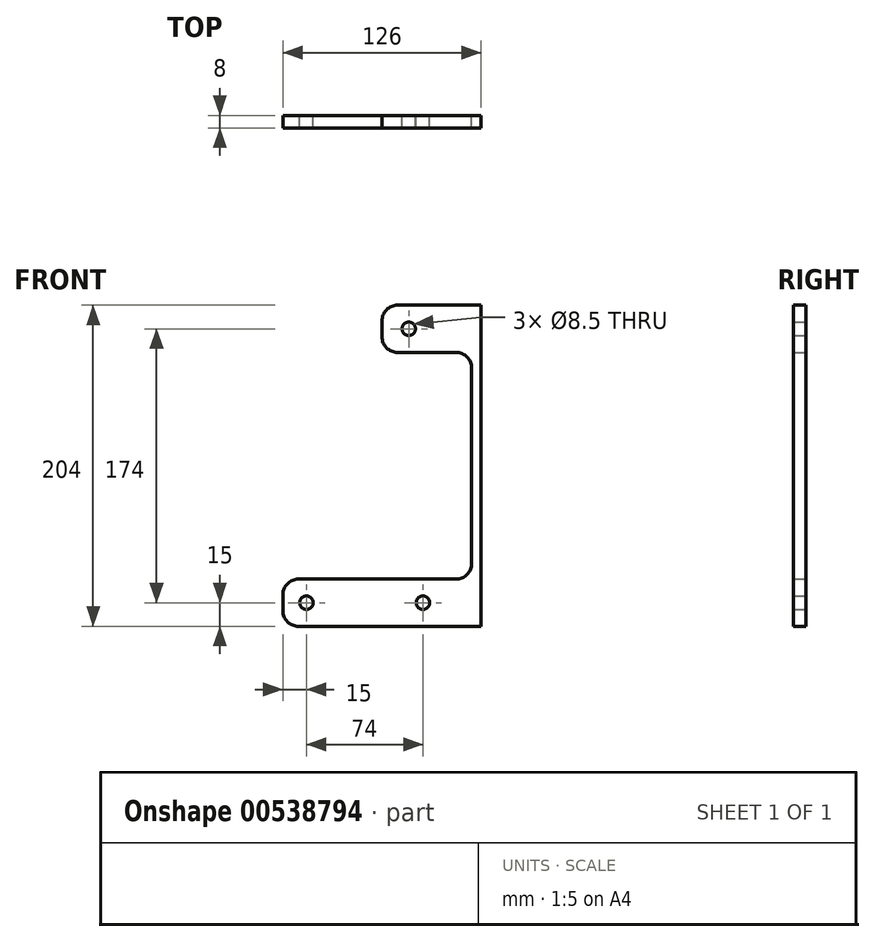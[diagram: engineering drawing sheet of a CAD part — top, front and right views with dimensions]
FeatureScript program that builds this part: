
annotation { "Feature Type Name" : "Feature", "Feature Type Description" : "" }
export const myFeature = defineFeature(function(context is Context, id is Id, definition is map)
    precondition{}
    {
        {
            var Q0;
            Q0=qCreatedBy(makeId("Front.planeOp"),FACE);
            var sketch = newSketch(context, id + "F0", { "sketchPlane" : qUnion([Q0])});
            skLineSegment(sketch, "E0", {"start": v(0, 0) * mm, "end": v(0, -183.01) * mm});
            skCircle(sketch, "E1", {"center": v(-46, 0) * mm, "radius": 4.25 * mm});
            skCircle(sketch, "E2", {"center": v(-37, -174) * mm, "radius": 4.25 * mm});
            skCircle(sketch, "E3", {"center": v(-111, -174) * mm, "radius": 4.25 * mm});
            skLineSegment(sketch, "E4", {"start": v(0, 0) * mm, "end": v(0, 15) * mm});
            skLineSegment(sketch, "E5", {"start": v(0, 15) * mm, "end": v(-53, 15) * mm});
            skLineSegment(sketch, "E6", {"start": v(-126, -169) * mm, "end": v(-126, -179) * mm});
            skLineSegment(sketch, "E7", {"start": v(-116, -189) * mm, "end": v(0, -189) * mm});
            skLineSegment(sketch, "E8", {"start": v(0, -189) * mm, "end": v(0, -183.01) * mm});
            skLineSegment(sketch, "E9", {"start": v(-116, -159) * mm, "end": v(-22.58, -159) * mm});
            skLineSegment(sketch, "E10", {"start": v(-63, 5) * mm, "end": v(-63, -5) * mm});
            skLineSegment(sketch, "E11", {"start": v(-53, -15) * mm, "end": v(-16, -15) * mm});
            skPoint(sketch, "E12.orphan", {"position": v(-126, 15) * mm});
            skLineSegment(sketch, "E13", {"start": v(-6, -25) * mm, "end": v(-6, -149) * mm});
            skLineSegment(sketch, "E14", {"start": v(-16, -159) * mm, "end": v(-22.58, -159) * mm});
            skPoint(sketch, "E15.visualSharp", {"position": v(-63, 15) * mm});
            skArc(sketch, "E15.filletArc", {"start": v(-53, 15) * mm, "mid": v(-60.07, 12.07) * mm, "end": v(-63, 5) * mm});
            skPoint(sketch, "E16.visualSharp", {"position": v(-63, -15) * mm});
            skArc(sketch, "E16.filletArc", {"start": v(-63, -5) * mm, "mid": v(-60.07, -12.07) * mm, "end": v(-53, -15) * mm});
            skPoint(sketch, "E17.visualSharp", {"position": v(-126, -159) * mm});
            skArc(sketch, "E17.filletArc", {"start": v(-116, -159) * mm, "mid": v(-123.07, -161.93) * mm, "end": v(-126, -169) * mm});
            skPoint(sketch, "E18.visualSharp", {"position": v(-126, -189) * mm});
            skArc(sketch, "E18.filletArc", {"start": v(-126, -179) * mm, "mid": v(-123.07, -186.07) * mm, "end": v(-116, -189) * mm});
            skPoint(sketch, "E19.visualSharp", {"position": v(-6, -159) * mm});
            skArc(sketch, "E19.filletArc", {"start": v(-16, -159) * mm, "mid": v(-8.93, -156.07) * mm, "end": v(-6, -149) * mm});
            skPoint(sketch, "E20.visualSharp", {"position": v(-6, -15) * mm});
            skArc(sketch, "E20.filletArc", {"start": v(-6, -25) * mm, "mid": v(-8.93, -17.93) * mm, "end": v(-16, -15) * mm});
            skSolve(sketch);
        }
        {
            var Q0;
            Q0=makeQuery(id+"F0.imprint","IMPRINT",FACE,{"disambiguationData":[TD([[makeQuery(id+"F0.imprint","IMPRINT",EDGE,{"derivedFrom":sQuery(id+"F0.wireOp",EDGE,"E0")}),-1.0]])]});
            extrude(context, id + "F1", {"entities" : qUnion([Q0]), "depth" : 8 * mm, "offsetDistance" : 25 * mm});
        }
    });
